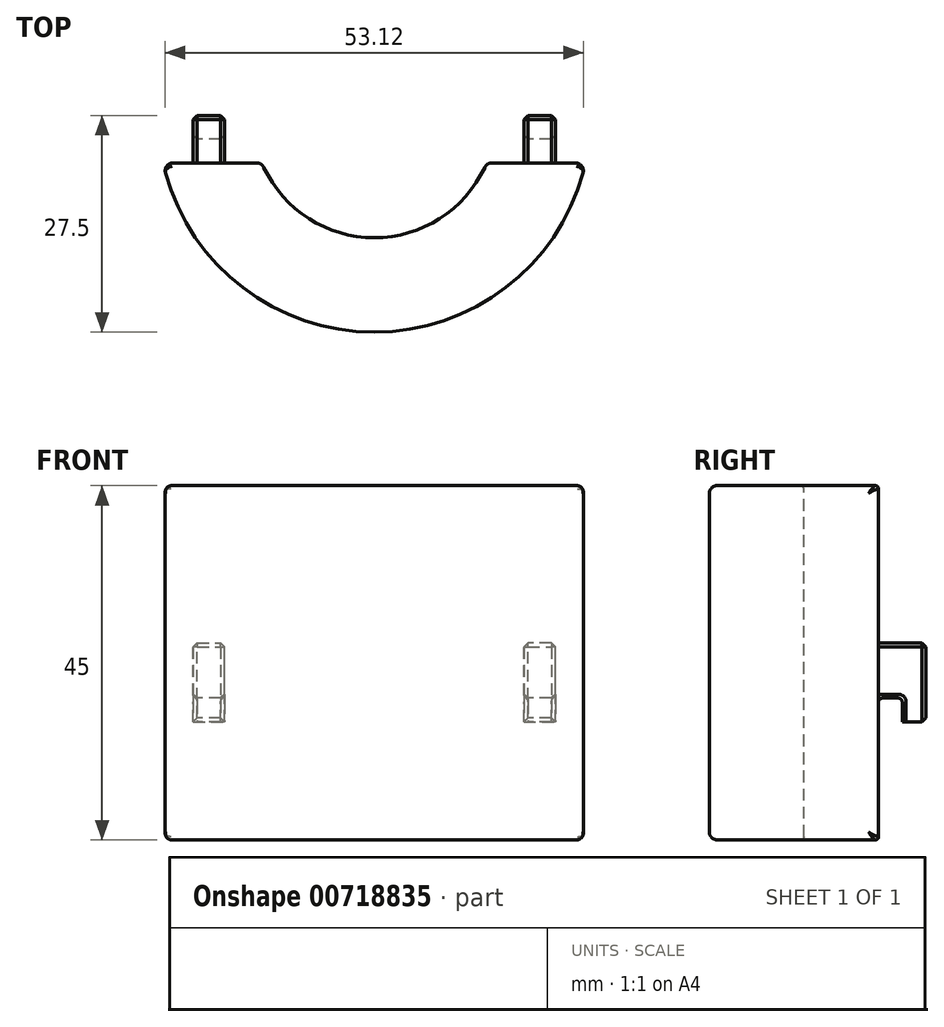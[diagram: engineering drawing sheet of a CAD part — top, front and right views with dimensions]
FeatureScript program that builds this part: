
annotation { "Feature Type Name" : "Feature", "Feature Type Description" : "" }
export const myFeature = defineFeature(function(context is Context, id is Id, definition is map)
    precondition{}
    {
        {
            var Q0;
            Q0=qCreatedBy(makeId("Top.planeOp"),FACE);
            var sketch = newSketch(context, id + "F0", { "sketchPlane" : qUnion([Q0])});
            skArc(sketch, "E0", {"start": v(-14.3, -36) * mm, "mid": v(0, -45.5) * mm, "end": v(14.3, -36) * mm});
            skArc(sketch, "E1", {"start": v(-26.84, -36) * mm, "mid": v(0, -57.5) * mm, "end": v(26.84, -36) * mm});
            skLineSegment(sketch, "E2", {"start": v(-26.84, -36) * mm, "end": v(-14.3, -36) * mm});
            skLineSegment(sketch, "E3.trimOffspring", {"start": v(14.3, -36) * mm, "end": v(26.84, -36) * mm});
            skSolve(sketch);
        }
        {
            var Q0;
            Q0 = qSketchRegion(id + "F0", true);
            extrude(context, id + "F1", {"entities" : qUnion([Q0]), "oppositeDirection" : true, "depth" : 45 * mm, "offsetDistance" : 25 * mm});
        }
        {
            var Q0;
            Q0=makeQuery(id+"F1.opExtrude","CAP_EDGE",EDGE,{"disambiguationData":[OSD([sQuery(id+"F0.wireOp",EDGE,"E1")])],"isStart":false});
            var Q1;
            Q1=makeQuery(id+"F1.opExtrude","SWEPT_EDGE",EDGE,{"disambiguationData":[OSD([sQuery(id+"F0.wireOp",EDGE,"E1"),sQuery(id+"F0.wireOp",EDGE,"E2")])]});
            var Q2;
            Q2=makeQuery(id+"F1.opExtrude","CAP_EDGE",EDGE,{"disambiguationData":[OSD([sQuery(id+"F0.wireOp",EDGE,"E1")])],"isStart":true});
            var Q3;
            Q3=makeQuery(id+"F1.opExtrude","SWEPT_EDGE",EDGE,{"disambiguationData":[OSD([sQuery(id+"F0.wireOp",EDGE,"E1"),sQuery(id+"F0.wireOp",EDGE,"E3.trimOffspring")])]});
            var Q4;
            Q4=makeQuery(id+"F1.opExtrude","SWEPT_EDGE",EDGE,{"disambiguationData":[OSD([sQuery(id+"F0.wireOp",EDGE,"E0"),sQuery(id+"F0.wireOp",EDGE,"E2")])]});
            var Q5;
            Q5=makeQuery(id+"F1.opExtrude","SWEPT_EDGE",EDGE,{"disambiguationData":[OSD([sQuery(id+"F0.wireOp",EDGE,"E0"),sQuery(id+"F0.wireOp",EDGE,"E3.trimOffspring")])]});
            fillet(context, id + "F2", {"entities" : qUnion([Q0, Q1, Q2, Q3, Q4, Q5]), "radius" : 1 * mm, "tangentPropagation" : true, "allowEdgeOverflow" : false});
        }
        {
            var Q0;
            Q0=makeQuery(id+"F1.opExtrude","CAP_EDGE",EDGE,{"disambiguationData":[OSD([sQuery(id+"F0.wireOp",EDGE,"E0")])],"isStart":true});
            var Q1;
            Q1=makeQuery(id+"F1.opExtrude","CAP_EDGE",EDGE,{"disambiguationData":[OSD([sQuery(id+"F0.wireOp",EDGE,"E0")])],"isStart":false});
            fillet(context, id + "F3", {"entities" : qUnion([Q0, Q1]), "radius" : 0.4 * mm, "tangentPropagation" : true, "allowEdgeOverflow" : false});
        }
        {
            var Q0;
            Q0=makeQuery(id+"F1.opExtrude","CAP_FACE",FACE,{"disambiguationData":[OSD([sQuery(id+"F0.wireOp",EDGE,"E0"),sQuery(id+"F0.wireOp",EDGE,"E1"),sQuery(id+"F0.wireOp",EDGE,"E2"),sQuery(id+"F0.wireOp",EDGE,"E3.trimOffspring")])],"isStart":true});
            var sketch = newSketch(context, id + "F4", { "sketchPlane" : qUnion([Q0])});
            skLineSegment(sketch, "E4.bottom", {"start": v(-23, -30) * mm, "end": v(-19, -30) * mm});
            skLineSegment(sketch, "E4.top", {"start": v(-23, -36) * mm, "end": v(-19, -36) * mm});
            skLineSegment(sketch, "E4.left", {"start": v(-23, -30) * mm, "end": v(-23, -36) * mm});
            skLineSegment(sketch, "E4.right", {"start": v(-19, -30) * mm, "end": v(-19, -36) * mm});
            skLineSegment(sketch, "E5.MirrorCS", {"start": v(19, -30) * mm, "end": v(19, -36) * mm});
            skLineSegment(sketch, "E6.MirrorCS", {"start": v(23, -30) * mm, "end": v(19, -30) * mm});
            skLineSegment(sketch, "E7.MirrorCS", {"start": v(23, -30) * mm, "end": v(23, -36) * mm});
            skLineSegment(sketch, "E8.MirrorCS", {"start": v(23, -36) * mm, "end": v(19, -36) * mm});
            skSolve(sketch);
        }
        {
            var Q0;
            Q0 = qSketchRegion(id + "F4", true);
            extrude(context, id + "F5", {"entities" : qUnion([Q0]), "operationType" : NewBodyOperationType.ADD, "oppositeDirection" : true, "depth" : 30 * mm, "offsetDistance" : 25 * mm, "hasSecondDirection" : true, "secondDirectionOppositeDirection" : true, "secondDirectionDepth" : 20 * mm});
        }
        {
            var Q0;
            Q0=qCreatedBy(makeId("Right.planeOp"),FACE);
            var sketch = newSketch(context, id + "F6", { "sketchPlane" : qUnion([Q0])});
            skLineSegment(sketch, "E9.bottom", {"start": v(-33, -30) * mm, "end": v(-36, -30) * mm});
            skLineSegment(sketch, "E9.top", {"start": v(-33, -27) * mm, "end": v(-36, -27) * mm});
            skLineSegment(sketch, "E9.left", {"start": v(-33, -30) * mm, "end": v(-33, -27) * mm});
            skLineSegment(sketch, "E9.right", {"start": v(-36, -30) * mm, "end": v(-36, -27) * mm});
            skSolve(sketch);
        }
        {
            var Q0;
            Q0=makeQuery(id+"F6.imprint","IMPRINT",FACE,{"disambiguationData":[TD([[makeQuery(id+"F6.imprint","IMPRINT",EDGE,{"derivedFrom":sQuery(id+"F6.wireOp",EDGE,"E9.bottom")}),-1.0]])]});
            extrude(context, id + "F7", {"entities" : qUnion([Q0]), "endBound" : BoundingType.SYMMETRIC, "depth" : 90 * mm, "offsetDistance" : 25 * mm});
        }
        {
            var Q0;
            Q0=makeQuery(id+"F7.opExtrude","SWEPT_BODY",BODY,{"disambiguationData":[OSD([sQuery(id+"F6.wireOp",EDGE,"E9.bottom"),sQuery(id+"F6.wireOp",EDGE,"E9.top"),sQuery(id+"F6.wireOp",EDGE,"E9.left"),sQuery(id+"F6.wireOp",EDGE,"E9.right")])]});
            var Q1;
            Q1=makeQuery(id+"F1.opExtrude","SWEPT_BODY",BODY,{"disambiguationData":[OSD([sQuery(id+"F0.wireOp",EDGE,"E0"),sQuery(id+"F0.wireOp",EDGE,"E1"),sQuery(id+"F0.wireOp",EDGE,"E2"),sQuery(id+"F0.wireOp",EDGE,"E3.trimOffspring")])]});
            booleanBodies(context, id + "F8", {"operationType" : BooleanOperationType.SUBTRACTION, "tools" : qUnion([Q0]), "targets" : qUnion([Q1])});
        }
        {
            var Q0;
            Q0=makeQuery(id+"F5.opExtrude","CAP_EDGE",EDGE,{"disambiguationData":[OSD([sQuery(id+"F4.wireOp",EDGE,"E4.top")])],"isStart":true});
            var Q1;
            Q1=makeQuery(id+"F5.opExtrude","CAP_EDGE",EDGE,{"disambiguationData":[OSD([sQuery(id+"F4.wireOp",EDGE,"E8.MirrorCS")])],"isStart":true});
            var Q2;
            Q2=makeQuery(id+"F5.opExtrude","SWEPT_EDGE",EDGE,{"disambiguationData":[OSD([sQuery(id+"F4.wireOp",EDGE,"E5.MirrorCS"),sQuery(id+"F4.wireOp",EDGE,"E8.MirrorCS")])]});
            var Q3;
            Q3=makeQuery(id+"F5.opExtrude","SWEPT_EDGE",EDGE,{"disambiguationData":[OSD([sQuery(id+"F4.wireOp",EDGE,"E4.top"),sQuery(id+"F4.wireOp",EDGE,"E4.left")])]});
            var Q4;
            Q4=makeQuery(id+"F5.opExtrude","SWEPT_EDGE",EDGE,{"disambiguationData":[OSD([sQuery(id+"F4.wireOp",EDGE,"E7.MirrorCS"),sQuery(id+"F4.wireOp",EDGE,"E8.MirrorCS")])]});
            var Q5;
            Q5=makeQuery(id+"F5.opExtrude","SWEPT_EDGE",EDGE,{"disambiguationData":[OSD([sQuery(id+"F4.wireOp",EDGE,"E4.top"),sQuery(id+"F4.wireOp",EDGE,"E4.right")])]});
            var Q6;
            {var subQ0=sQuery(id+"F6.wireOp",EDGE,"E9.right");var subQ1=sQuery(id+"F6.wireOp",EDGE,"E9.top");Q6=makeQuery(id+"F8.opBoolean","COPY",EDGE,{"disambiguationData":[topologyDisambiguationEdgeConnected([makeQuery(id+"F1.opExtrude","SWEPT_FACE",FACE,{"disambiguationData":[OSD([sQuery(id+"F0.wireOp",EDGE,"E3.trimOffspring")])]})])],"derivedFrom":makeQuery(id+"F7.opExtrude","SWEPT_EDGE",EDGE,{"disambiguationData":[OSD([subQ1,subQ0])]})});}
            var Q7;
            {var subQ0=sQuery(id+"F6.wireOp",EDGE,"E9.top");var subQ1=sQuery(id+"F6.wireOp",EDGE,"E9.right");Q7=makeQuery(id+"F8.opBoolean","COPY",EDGE,{"disambiguationData":[topologyDisambiguationEdgeConnected([makeQuery(id+"F1.opExtrude","SWEPT_FACE",FACE,{"disambiguationData":[OSD([sQuery(id+"F0.wireOp",EDGE,"E2")])]})])],"derivedFrom":makeQuery(id+"F7.opExtrude","SWEPT_EDGE",EDGE,{"disambiguationData":[OSD([subQ0,subQ1])]})});}
            var Q8;
            {var subQ0=sQuery(id+"F6.wireOp",EDGE,"E9.top");var subQ1=sQuery(id+"F6.wireOp",EDGE,"E9.left");Q8=makeQuery(id+"F8.opBoolean","COPY",EDGE,{"disambiguationData":[TD([makeQuery(id+"F5.opExtrude","SWEPT_FACE",FACE,{"disambiguationData":[OSD([sQuery(id+"F4.wireOp",EDGE,"E5.MirrorCS")])]})])],"derivedFrom":makeQuery(id+"F7.opExtrude","SWEPT_EDGE",EDGE,{"disambiguationData":[OSD([subQ0,subQ1])]})});}
            var Q9;
            {var subQ0=sQuery(id+"F6.wireOp",EDGE,"E9.left");var subQ1=sQuery(id+"F6.wireOp",EDGE,"E9.top");Q9=makeQuery(id+"F8.opBoolean","COPY",EDGE,{"disambiguationData":[TD([makeQuery(id+"F5.opExtrude","SWEPT_FACE",FACE,{"disambiguationData":[OSD([sQuery(id+"F4.wireOp",EDGE,"E4.left")])]})])],"derivedFrom":makeQuery(id+"F7.opExtrude","SWEPT_EDGE",EDGE,{"disambiguationData":[OSD([subQ1,subQ0])]})});}
            fillet(context, id + "F9", {"entities" : qUnion([Q0, Q1, Q2, Q3, Q4, Q5, Q6, Q7, Q8, Q9]), "radius" : 0.5 * mm, "tangentPropagation" : true, "allowEdgeOverflow" : false});
        }
        {
            var Q0;
            Q0=makeQuery(id+"F5.opExtrude","SWEPT_EDGE",EDGE,{"disambiguationData":[OSD([sQuery(id+"F4.wireOp",EDGE,"E6.MirrorCS"),sQuery(id+"F4.wireOp",EDGE,"E7.MirrorCS")])]});
            var Q1;
            Q1=makeQuery(id+"F5.opExtrude","SWEPT_EDGE",EDGE,{"disambiguationData":[OSD([sQuery(id+"F4.wireOp",EDGE,"E4.bottom"),sQuery(id+"F4.wireOp",EDGE,"E4.right")])]});
            var Q2;
            Q2=makeQuery(id+"F5.opExtrude","SWEPT_EDGE",EDGE,{"disambiguationData":[OSD([sQuery(id+"F4.wireOp",EDGE,"E5.MirrorCS"),sQuery(id+"F4.wireOp",EDGE,"E6.MirrorCS")])]});
            var Q3;
            Q3=makeQuery(id+"F5.opExtrude","SWEPT_EDGE",EDGE,{"disambiguationData":[OSD([sQuery(id+"F4.wireOp",EDGE,"E4.bottom"),sQuery(id+"F4.wireOp",EDGE,"E4.left")])]});
            var Q4;
            Q4=makeQuery(id+"F5.opExtrude","CAP_EDGE",EDGE,{"disambiguationData":[OSD([sQuery(id+"F4.wireOp",EDGE,"E4.bottom")])],"isStart":true});
            var Q5;
            Q5=makeQuery(id+"F5.opExtrude","CAP_EDGE",EDGE,{"disambiguationData":[OSD([sQuery(id+"F4.wireOp",EDGE,"E4.bottom")])],"isStart":false});
            var Q6;
            Q6=makeQuery(id+"F5.opExtrude","CAP_EDGE",EDGE,{"disambiguationData":[OSD([sQuery(id+"F4.wireOp",EDGE,"E6.MirrorCS")])],"isStart":false});
            var Q7;
            Q7=makeQuery(id+"F5.opExtrude","CAP_EDGE",EDGE,{"disambiguationData":[OSD([sQuery(id+"F4.wireOp",EDGE,"E6.MirrorCS")])],"isStart":true});
            var Q8;
            Q8=makeQuery(id+"F5.opExtrude","CAP_EDGE",EDGE,{"disambiguationData":[OSD([sQuery(id+"F4.wireOp",EDGE,"E5.MirrorCS")])],"isStart":true});
            var Q9;
            Q9=makeQuery(id+"F5.opExtrude","CAP_EDGE",EDGE,{"disambiguationData":[OSD([sQuery(id+"F4.wireOp",EDGE,"E7.MirrorCS")])],"isStart":true});
            var Q10;
            Q10=makeQuery(id+"F5.opExtrude","CAP_EDGE",EDGE,{"disambiguationData":[OSD([sQuery(id+"F4.wireOp",EDGE,"E4.right")])],"isStart":true});
            var Q11;
            Q11=makeQuery(id+"F5.opExtrude","CAP_EDGE",EDGE,{"disambiguationData":[OSD([sQuery(id+"F4.wireOp",EDGE,"E4.left")])],"isStart":true});
            chamfer(context, id + "F10", {"entities" : qUnion([Q0, Q1, Q2, Q3, Q4, Q5, Q6, Q7, Q8, Q9, Q10, Q11]), "width" : 0.5 * mm, "tangentPropagation" : true});
        }
        {
            var Q0;
            Q0=makeQuery(id+"F8.opBoolean","INTERSECT",EDGE,{"derivedFrom":[makeQuery(id+"F5.opExtrude","SWEPT_FACE",FACE,{"disambiguationData":[OSD([sQuery(id+"F4.wireOp",EDGE,"E7.MirrorCS")])]}),makeQuery(id+"F7.opExtrude","SWEPT_FACE",FACE,{"disambiguationData":[OSD([sQuery(id+"F6.wireOp",EDGE,"E9.top")])]})]});
            var Q1;
            Q1=makeQuery(id+"F8.opBoolean","INTERSECT",EDGE,{"derivedFrom":[makeQuery(id+"F5.opExtrude","SWEPT_FACE",FACE,{"disambiguationData":[OSD([sQuery(id+"F4.wireOp",EDGE,"E5.MirrorCS")])]}),makeQuery(id+"F7.opExtrude","SWEPT_FACE",FACE,{"disambiguationData":[OSD([sQuery(id+"F6.wireOp",EDGE,"E9.top")])]})]});
            var Q2;
            Q2=makeQuery(id+"F8.opBoolean","INTERSECT",EDGE,{"derivedFrom":[makeQuery(id+"F5.opExtrude","SWEPT_FACE",FACE,{"disambiguationData":[OSD([sQuery(id+"F4.wireOp",EDGE,"E4.right")])]}),makeQuery(id+"F7.opExtrude","SWEPT_FACE",FACE,{"disambiguationData":[OSD([sQuery(id+"F6.wireOp",EDGE,"E9.top")])]})]});
            var Q3;
            Q3=makeQuery(id+"F8.opBoolean","INTERSECT",EDGE,{"derivedFrom":[makeQuery(id+"F5.opExtrude","SWEPT_FACE",FACE,{"disambiguationData":[OSD([sQuery(id+"F4.wireOp",EDGE,"E4.left")])]}),makeQuery(id+"F7.opExtrude","SWEPT_FACE",FACE,{"disambiguationData":[OSD([sQuery(id+"F6.wireOp",EDGE,"E9.top")])]})]});
            chamfer(context, id + "F11", {"entities" : qUnion([Q0, Q1, Q2, Q3]), "width" : 0.5 * mm, "tangentPropagation" : true});
        }
    });
